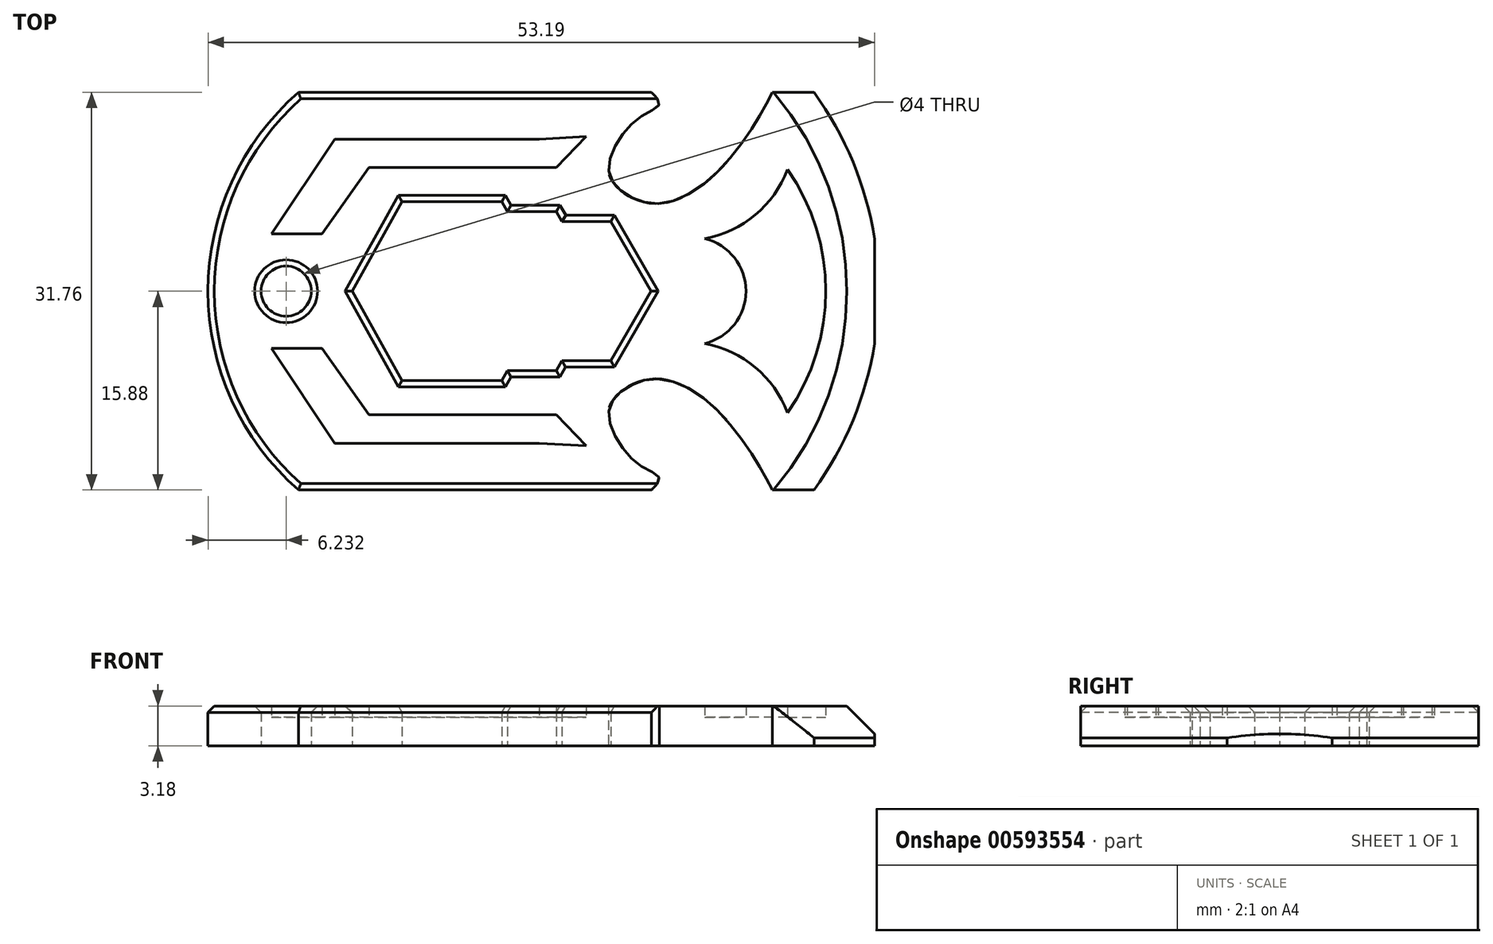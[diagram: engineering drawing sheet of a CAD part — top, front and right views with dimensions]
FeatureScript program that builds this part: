
annotation { "Feature Type Name" : "Feature", "Feature Type Description" : "" }
export const myFeature = defineFeature(function(context is Context, id is Id, definition is map)
    precondition{}
    {
        {
            var Q0;
            Q0=qCreatedBy(makeId("Top.planeOp"),FACE);
            var sketch = newSketch(context, id + "F0", { "sketchPlane" : qUnion([Q0])});
            skLineSegment(sketch, "E0.bottom", {"start": v(-25.4, 15.88) * mm, "end": v(25.4, 15.88) * mm});
            skLineSegment(sketch, "E0.top", {"start": v(-25.4, -15.87) * mm, "end": v(25.4, -15.87) * mm});
            skLineSegment(sketch, "E0.left", {"start": v(-25.4, 15.88) * mm, "end": v(-25.4, -15.87) * mm});
            skLineSegment(sketch, "E0.right", {"start": v(25.4, 15.87) * mm, "end": v(25.4, -15.87) * mm});
            skPoint(sketch, "E0.middle", {"position": v(0, 0) * mm});
            skLineSegment(sketch, "E1.MirrorCS", {"start": v(-76.2, 15.88) * mm, "end": v(-76.2, -15.87) * mm});
            skArc(sketch, "E2", {"start": v(-20.57, 15.87) * mm, "mid": v(-27.8, 0) * mm, "end": v(-20.57, -15.87) * mm});
            skArc(sketch, "E3", {"start": v(20.57, -15.87) * mm, "mid": v(25.72, 0) * mm, "end": v(20.57, 15.88) * mm});
            skCircle(sketch, "E4", {"center": v(-21.56, 0) * mm, "radius": 2 * mm});
            skLineSegment(sketch, "E5", {"start": v(-12.3, 7.14) * mm, "end": v(-16.27, 0) * mm});
            skLineSegment(sketch, "E6", {"start": v(-16.27, 0) * mm, "end": v(-12.3, -7.14) * mm});
            skLineSegment(sketch, "E7", {"start": v(-12.3, 7.14) * mm, "end": v(-4.35, 7.14) * mm});
            skLineSegment(sketch, "E8", {"start": v(-12.3, -7.14) * mm, "end": v(-4.35, -7.14) * mm});
            skLineSegment(sketch, "E9", {"start": v(-4.35, 7.14) * mm, "end": v(-3.9, 6.35) * mm});
            skLineSegment(sketch, "E10", {"start": v(-3.9, -6.35) * mm, "end": v(-4.35, -7.14) * mm});
            skLineSegment(sketch, "E11", {"start": v(-3.9, 6.35) * mm, "end": v(0, 6.35) * mm});
            skLineSegment(sketch, "E12", {"start": v(-3.9, -6.35) * mm, "end": v(0, -6.35) * mm});
            skLineSegment(sketch, "E13", {"start": v(0, 6.35) * mm, "end": v(0.46, 5.55) * mm});
            skLineSegment(sketch, "E14", {"start": v(0, -6.35) * mm, "end": v(0.46, -5.56) * mm});
            skLineSegment(sketch, "E15", {"start": v(0.46, 5.55) * mm, "end": v(4.35, 5.55) * mm});
            skLineSegment(sketch, "E16", {"start": v(0.46, -5.56) * mm, "end": v(4.34, -5.56) * mm});
            skLineSegment(sketch, "E17", {"start": v(4.35, 5.55) * mm, "end": v(7.56, 0) * mm});
            skLineSegment(sketch, "E18", {"start": v(4.34, -5.56) * mm, "end": v(7.56, 0) * mm});
            skArc(sketch, "E19", {"start": v(19.55, -15.88) * mm, "mid": v(24.54, 0) * mm, "end": v(19.55, 15.88) * mm});
            skFitSpline(sketch, "E20", {"points": [v(17.26, 15.87) * mm, v(15.73, 13.2) * mm, v(12.32, 9.02) * mm, v(8.3, 7) * mm, v(5.52, 7.77) * mm, v(4.2, 9.5) * mm, v(5.03, 12.15) * mm, v(6.97, 14.1) * mm, v(8.22, 14.93) * mm, v(7.6, 15.87) * mm], "startDerivative": vector(-11.4, -21.47) * mm, "endDerivative": vector(-14.56, 14.4) * mm});
            skFitSpline(sketch, "E21.MirrorCS", {"points": [v(17.26, -15.88) * mm, v(15.73, -13.2) * mm, v(12.32, -9.02) * mm, v(8.3, -7) * mm, v(5.52, -7.77) * mm, v(4.2, -9.5) * mm, v(5.03, -12.15) * mm, v(6.97, -14.1) * mm, v(8.22, -14.93) * mm, v(7.6, -15.88) * mm], "startDerivative": vector(-11.4, 21.47) * mm, "endDerivative": vector(-14.56, -14.4) * mm});
            skLineSegment(sketch, "E22", {"start": v(2.4, -12.34) * mm, "end": v(0, -9.88) * mm});
            skPoint(sketch, "E22.startSnap0", {"position": v(2.4, -5.56) * mm});
            skLineSegment(sketch, "E23", {"start": v(0, -9.88) * mm, "end": v(-14.96, -9.88) * mm});
            skLineSegment(sketch, "E24", {"start": v(-14.96, -9.88) * mm, "end": v(-18.7, -4.58) * mm});
            skLineSegment(sketch, "E25", {"start": v(-18.7, -4.58) * mm, "end": v(-22.72, -4.58) * mm});
            skLineSegment(sketch, "E26", {"start": v(-22.72, -4.58) * mm, "end": v(-17.67, -12.15) * mm});
            skLineSegment(sketch, "E27", {"start": v(-17.67, -12.15) * mm, "end": v(-1.36, -12.15) * mm});
            skLineSegment(sketch, "E28", {"start": v(-1.36, -12.15) * mm, "end": v(2.4, -12.34) * mm});
            skLineSegment(sketch, "E29.MirrorCS", {"start": v(-18.7, 4.58) * mm, "end": v(-22.72, 4.58) * mm});
            skLineSegment(sketch, "E30.MirrorCS", {"start": v(-14.96, 9.88) * mm, "end": v(-18.7, 4.58) * mm});
            skLineSegment(sketch, "E31.MirrorCS", {"start": v(-22.72, 4.58) * mm, "end": v(-17.67, 12.15) * mm});
            skLineSegment(sketch, "E32.MirrorCS", {"start": v(-17.67, 12.15) * mm, "end": v(-1.36, 12.15) * mm});
            skLineSegment(sketch, "E33.MirrorCS", {"start": v(-1.36, 12.15) * mm, "end": v(2.4, 12.34) * mm});
            skLineSegment(sketch, "E34.MirrorCS", {"start": v(2.4, 12.34) * mm, "end": v(0, 9.88) * mm});
            skLineSegment(sketch, "E35.MirrorCS", {"start": v(0, 9.88) * mm, "end": v(-14.96, 9.88) * mm});
            skArc(sketch, "E36", {"start": v(11.85, -4.18) * mm, "mid": v(15.14, 0) * mm, "end": v(11.85, 4.2) * mm});
            skArc(sketch, "E37", {"start": v(18.47, -9.7) * mm, "mid": v(15.88, -6.08) * mm, "end": v(11.85, -4.18) * mm});
            skArc(sketch, "E38.MirrorCS", {"start": v(18.47, 9.71) * mm, "mid": v(15.88, 6.1) * mm, "end": v(11.85, 4.2) * mm});
            skArc(sketch, "E39", {"start": v(18.47, -9.7) * mm, "mid": v(21.51, 0) * mm, "end": v(18.47, 9.71) * mm});
            skSolve(sketch);
        }
        {
            var Q0;
            {var subQ0=sQuery(id+"F0.wireOp",EDGE,"E2");var subQ1=sQuery(id+"F0.wireOp",EDGE,"E0.left");var subQ2=makeQuery(id+"F0.imprint","INTERSECT",VERTEX,{"disambiguationData":[OD(0.0)],"derivedFrom":[subQ1,subQ0]});Q0=makeQuery(id+"F0.imprint","IMPRINT",FACE,{"disambiguationData":[TD([[makeQuery(id+"F0.imprint","IMPRINT",EDGE,{"disambiguationData":[TD([[subQ2,-1.0]])],"derivedFrom":subQ1}),-1.0]])]});}
            var Q1;
            Q1=makeQuery(id+"F0.imprint","IMPRINT",FACE,{"disambiguationData":[TD([[makeQuery(id+"F0.imprint","IMPRINT",EDGE,{"derivedFrom":sQuery(id+"F0.wireOp",EDGE,"E4")}),-1.0]])]});
            var Q2;
            {var subQ0=sQuery(id+"F0.wireOp",EDGE,"E3");var subQ1=sQuery(id+"F0.wireOp",EDGE,"E0.right");var subQ2=makeQuery(id+"F0.imprint","INTERSECT",VERTEX,{"disambiguationData":[OD(0.0)],"derivedFrom":[subQ1,subQ0]});Q2=makeQuery(id+"F0.imprint","IMPRINT",FACE,{"disambiguationData":[TD([[makeQuery(id+"F0.imprint","IMPRINT",EDGE,{"disambiguationData":[TD([[subQ2,-1.0]])],"derivedFrom":subQ1}),1.0]])]});}
            var Q3;
            {var subQ5=sQuery(id+"F0.wireOp",EDGE,"E19");Q3=makeQuery(id+"F0.imprint","IMPRINT",FACE,{"disambiguationData":[TD([[makeQuery(id+"F0.imprint","IMPRINT",EDGE,{"derivedFrom":subQ5}),-1.0]])]});}
            extrude(context, id + "F1", {"entities" : qUnion([Q0, Q1, Q2, Q3]), "depth" : 3.17 * mm, "offsetDistance" : 25.4 * mm});
        }
        {
            var Q0;
            Q0=makeQuery(id+"F1.opExtrude","CAP_EDGE",EDGE,{"disambiguationData":[OSD([sQuery(id+"F0.wireOp",EDGE,"E3")])],"isStart":false});
            chamfer(context, id + "F2", {"entities" : qUnion([Q0]), "chamferType" : ChamferType.TWO_OFFSETS, "width1" : 2.54 * mm, "oppositeDirection" : false, "width2" : 2.54 * mm, "tangentPropagation" : true});
        }
        {
            var Q0;
            Q0=makeQuery(id+"F1.opExtrude","CAP_EDGE",EDGE,{"disambiguationData":[OSD([sQuery(id+"F0.wireOp",EDGE,"E4")])],"isStart":false});
            var Q1;
            Q1=makeQuery(id+"F1.opExtrude","CAP_EDGE",EDGE,{"disambiguationData":[OSD([sQuery(id+"F0.wireOp",EDGE,"E5")])],"isStart":false});
            var Q2;
            Q2=makeQuery(id+"F1.opExtrude","CAP_EDGE",EDGE,{"disambiguationData":[OSD([sQuery(id+"F0.wireOp",EDGE,"E6")])],"isStart":false});
            var Q3;
            Q3=makeQuery(id+"F1.opExtrude","CAP_EDGE",EDGE,{"disambiguationData":[OSD([sQuery(id+"F0.wireOp",EDGE,"E8")])],"isStart":false});
            var Q4;
            Q4=makeQuery(id+"F1.opExtrude","CAP_EDGE",EDGE,{"disambiguationData":[OSD([sQuery(id+"F0.wireOp",EDGE,"E7")])],"isStart":false});
            var Q5;
            Q5=makeQuery(id+"F1.opExtrude","CAP_EDGE",EDGE,{"disambiguationData":[OSD([sQuery(id+"F0.wireOp",EDGE,"E10")])],"isStart":false});
            var Q6;
            Q6=makeQuery(id+"F1.opExtrude","CAP_EDGE",EDGE,{"disambiguationData":[OSD([sQuery(id+"F0.wireOp",EDGE,"E12")])],"isStart":false});
            var Q7;
            Q7=makeQuery(id+"F1.opExtrude","CAP_EDGE",EDGE,{"disambiguationData":[OSD([sQuery(id+"F0.wireOp",EDGE,"E14")])],"isStart":false});
            var Q8;
            Q8=makeQuery(id+"F1.opExtrude","CAP_EDGE",EDGE,{"disambiguationData":[OSD([sQuery(id+"F0.wireOp",EDGE,"E16")])],"isStart":false});
            var Q9;
            Q9=makeQuery(id+"F1.opExtrude","CAP_EDGE",EDGE,{"disambiguationData":[OSD([sQuery(id+"F0.wireOp",EDGE,"E18")])],"isStart":false});
            var Q10;
            Q10=makeQuery(id+"F1.opExtrude","CAP_EDGE",EDGE,{"disambiguationData":[OSD([sQuery(id+"F0.wireOp",EDGE,"E17")])],"isStart":false});
            var Q11;
            Q11=makeQuery(id+"F1.opExtrude","CAP_EDGE",EDGE,{"disambiguationData":[OSD([sQuery(id+"F0.wireOp",EDGE,"E9")])],"isStart":false});
            var Q12;
            Q12=makeQuery(id+"F1.opExtrude","CAP_EDGE",EDGE,{"disambiguationData":[OSD([sQuery(id+"F0.wireOp",EDGE,"E11")])],"isStart":false});
            var Q13;
            Q13=makeQuery(id+"F1.opExtrude","CAP_EDGE",EDGE,{"disambiguationData":[OSD([sQuery(id+"F0.wireOp",EDGE,"E13")])],"isStart":false});
            var Q14;
            Q14=makeQuery(id+"F1.opExtrude","CAP_EDGE",EDGE,{"disambiguationData":[OSD([sQuery(id+"F0.wireOp",EDGE,"E15")])],"isStart":false});
            var Q15;
            {var subQ0=sQuery(id+"F0.wireOp",EDGE,"E0.bottom");Q15=makeQuery(id+"F1.opExtrude","CAP_EDGE",EDGE,{"disambiguationData":[OSD([subQ0]),TDD([makeQuery(id+"F0.imprint","IMPRINT",EDGE,{"disambiguationData":[TD([[makeQuery(id+"F0.imprint","INTERSECT",VERTEX,{"derivedFrom":[subQ0,sQuery(id+"F0.wireOp",EDGE,"E2")]}),-1.0]])],"derivedFrom":subQ0})])],"isStart":false});}
            var Q16;
            Q16=makeQuery(id+"F1.opExtrude","CAP_EDGE",EDGE,{"disambiguationData":[OSD([sQuery(id+"F0.wireOp",EDGE,"E2")])],"isStart":false});
            var Q17;
            {var subQ0=sQuery(id+"F0.wireOp",EDGE,"E0.top");Q17=makeQuery(id+"F1.opExtrude","CAP_EDGE",EDGE,{"disambiguationData":[OSD([subQ0]),TDD([makeQuery(id+"F0.imprint","IMPRINT",EDGE,{"disambiguationData":[TD([[makeQuery(id+"F0.imprint","INTERSECT",VERTEX,{"derivedFrom":[subQ0,sQuery(id+"F0.wireOp",EDGE,"E2")]}),-1.0]])],"derivedFrom":subQ0})])],"isStart":false});}
            chamfer(context, id + "F3", {"entities" : qUnion([Q0, Q1, Q2, Q3, Q4, Q5, Q6, Q7, Q8, Q9, Q10, Q11, Q12, Q13, Q14, Q15, Q16, Q17]), "width" : 0.5 * mm, "tangentPropagation" : true});
        }
        {
            var Q0;
            Q0=makeQuery(id+"F0.imprint","IMPRINT",FACE,{"disambiguationData":[TD([[makeQuery(id+"F0.imprint","IMPRINT",EDGE,{"derivedFrom":sQuery(id+"F0.wireOp",EDGE,"E22")}),1.0]])]});
            var Q1;
            Q1=makeQuery(id+"F0.imprint","IMPRINT",FACE,{"disambiguationData":[TD([[makeQuery(id+"F0.imprint","IMPRINT",EDGE,{"derivedFrom":sQuery(id+"F0.wireOp",EDGE,"E29.MirrorCS")}),-1.0]])]});
            var Q2;
            Q2=makeQuery(id+"F0.imprint","IMPRINT",FACE,{"disambiguationData":[TD([[makeQuery(id+"F0.imprint","IMPRINT",EDGE,{"derivedFrom":sQuery(id+"F0.wireOp",EDGE,"86UBTqlr-tc8r-Cs0a-33Tu-CXogI8mYa14k")}),-1.0]])]});
            extrude(context, id + "F4", {"entities" : qUnion([Q0, Q1, Q2]), "operationType" : NewBodyOperationType.ADD, "depth" : 2.3 * mm, "offsetDistance" : 25.4 * mm});
        }
        {
            var Q0;
            Q0=makeQuery(id+"F0.imprint","IMPRINT",FACE,{"disambiguationData":[TD([[makeQuery(id+"F0.imprint","IMPRINT",EDGE,{"derivedFrom":sQuery(id+"F0.wireOp",EDGE,"E36")}),-1.0]])]});
            extrude(context, id + "F5", {"entities" : qUnion([Q0]), "operationType" : NewBodyOperationType.ADD, "depth" : 2.3 * mm, "offsetDistance" : 25.4 * mm});
        }
    });
